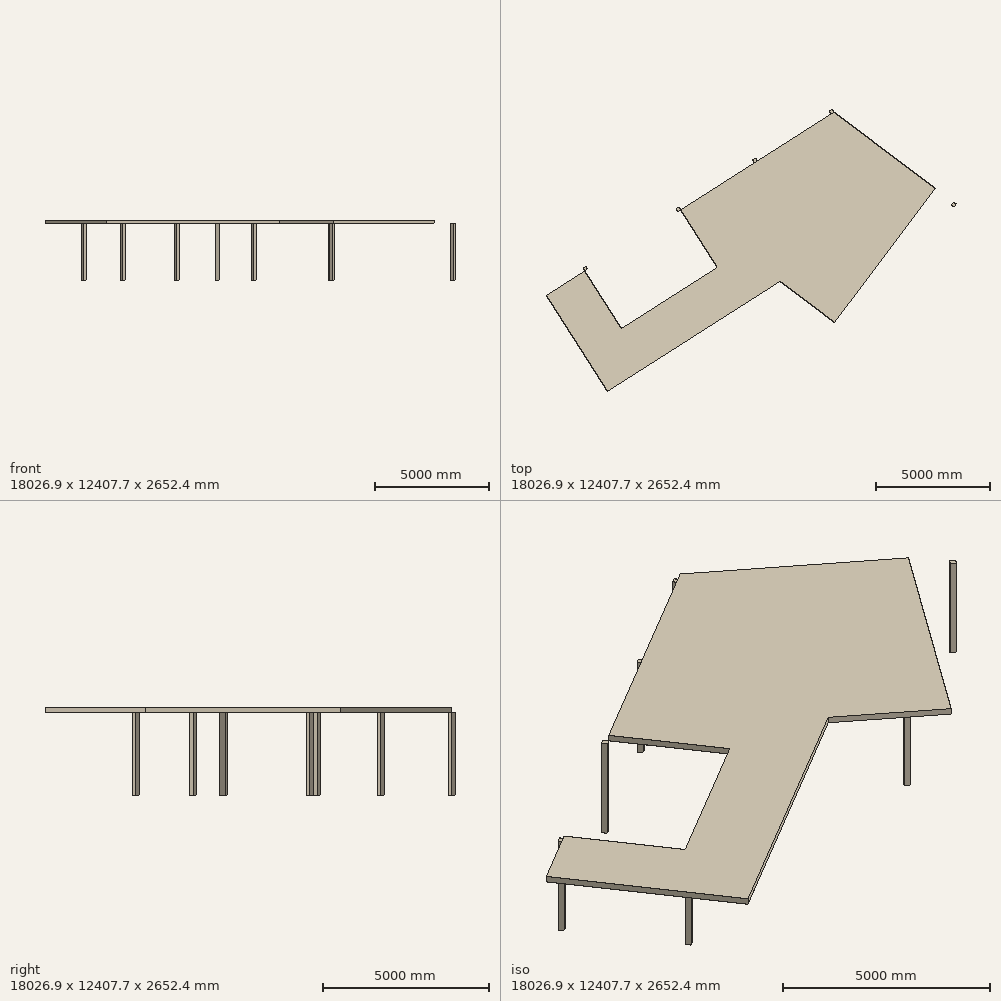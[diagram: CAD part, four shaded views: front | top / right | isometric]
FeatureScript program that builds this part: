
annotation { "Feature Type Name" : "Feature", "Feature Type Description" : "" }
export const myFeature = defineFeature(function(context is Context, id is Id, definition is map)
    precondition{}
    {
        {
            var Q0;
            Q0=qCreatedBy(makeId("Top.planeOp"),FACE);
            var sketch = newSketch(context, id + "F0", { "sketchPlane" : qUnion([Q0])});
            skLineSegment(sketch, "E0", {"start": v(-11635.93, 4721.16) * mm, "end": v(-8948.27, 504.95) * mm});
            skLineSegment(sketch, "E1", {"start": v(-8948.27, 504.95) * mm, "end": v(-1359.08, 5342.74) * mm});
            skLineSegment(sketch, "E2", {"start": v(-1359.08, 5342.74) * mm, "end": v(-4046.74, 9558.96) * mm});
            skLineSegment(sketch, "E3", {"start": v(-4046.74, 9558.96) * mm, "end": v(-5733.23, 8483.9) * mm});
            skLineSegment(sketch, "E4", {"start": v(-1359.08, 5342.74) * mm, "end": v(1038.57, 3539.62) * mm});
            skLineSegment(sketch, "E5", {"start": v(1038.57, 3539.62) * mm, "end": v(5469.96, 9432.14) * mm});
            skLineSegment(sketch, "E6", {"start": v(5469.96, 9432.14) * mm, "end": v(3072.3, 11235.27) * mm});
            skLineSegment(sketch, "E7", {"start": v(-4046.74, 9558.96) * mm, "end": v(1012.71, 12784.15) * mm});
            skLineSegment(sketch, "E8", {"start": v(1012.71, 12784.15) * mm, "end": v(3072.3, 11235.27) * mm});
            skLineSegment(sketch, "E9", {"start": v(-11098.4, 3877.92) * mm, "end": v(-9411.91, 4952.99) * mm});
            skLineSegment(sketch, "E10", {"start": v(-10560.87, 3034.68) * mm, "end": v(-8874.38, 4109.74) * mm});
            skLineSegment(sketch, "E11", {"start": v(-10023.33, 2191.43) * mm, "end": v(-8336.85, 3266.5) * mm});
            skLineSegment(sketch, "E12", {"start": v(-9485.8, 1348.2) * mm, "end": v(-1222.02, 6616) * mm});
            skLineSegment(sketch, "E13", {"start": v(239.36, 4140.66) * mm, "end": v(4670.74, 10033.19) * mm});
            skLineSegment(sketch, "E14", {"start": v(-559.86, 4741.7) * mm, "end": v(3871.52, 10634.23) * mm});
            skLineSegment(sketch, "E15", {"start": v(-10792.69, 5258.7) * mm, "end": v(-8105.03, 1042.48) * mm});
            skLineSegment(sketch, "E16", {"start": v(-9949.45, 5796.23) * mm, "end": v(-7261.78, 1580.01) * mm});
            skLineSegment(sketch, "E17", {"start": v(-7493.6, 3804.03) * mm, "end": v(-6418.54, 2117.55) * mm});
            skLineSegment(sketch, "E18", {"start": v(-6650.36, 4341.56) * mm, "end": v(-5575.3, 2655.08) * mm});
            skLineSegment(sketch, "E19", {"start": v(-5807.12, 4879.1) * mm, "end": v(-4732.05, 3192.61) * mm});
            skLineSegment(sketch, "E20", {"start": v(-4963.88, 5416.63) * mm, "end": v(-3888.81, 3730.14) * mm});
            skLineSegment(sketch, "E21", {"start": v(-5733.23, 8483.9) * mm, "end": v(-3045.57, 4267.68) * mm});
            skLineSegment(sketch, "E22", {"start": v(-4889.99, 9021.42) * mm, "end": v(-2202.32, 4805.2) * mm});
            skLineSegment(sketch, "E23.trimOffspring", {"start": v(-7493.6, 3804.03) * mm, "end": v(-1084.96, 7889.28) * mm});
            skLineSegment(sketch, "E24.trimOffspring", {"start": v(-9949.45, 5796.23) * mm, "end": v(-11635.93, 4721.16) * mm});
            skLineSegment(sketch, "E25.trimOffspring", {"start": v(-5195.7, 7640.65) * mm, "end": v(-810.83, 10435.82) * mm});
            skLineSegment(sketch, "E26.trimOffspring", {"start": v(-4658.16, 6797.4) * mm, "end": v(-947.9, 9162.55) * mm});
            skLineSegment(sketch, "E27", {"start": v(-8336.85, 3266.5) * mm, "end": v(-7493.6, 3804.03) * mm});
            skLineSegment(sketch, "E28", {"start": v(-1359.08, 5342.74) * mm, "end": v(3072.3, 11235.27) * mm});
            skPoint(sketch, "E29.orphan", {"position": v(0, 12138.59) * mm});
            skLineSegment(sketch, "E30", {"start": v(-1222.02, 6616) * mm, "end": v(1699.72, 4418.76) * mm});
            skLineSegment(sketch, "E31", {"start": v(-1084.96, 7889.28) * mm, "end": v(2360.86, 5297.9) * mm});
            skLineSegment(sketch, "E32", {"start": v(-947.9, 9162.55) * mm, "end": v(3022, 6177.04) * mm});
            skLineSegment(sketch, "E33", {"start": v(-810.83, 10435.82) * mm, "end": v(3683.15, 7056.18) * mm});
            skLineSegment(sketch, "E34", {"start": v(-673.77, 11709.09) * mm, "end": v(4344.3, 7935.32) * mm});
            skLineSegment(sketch, "E35", {"start": v(4945.34, 8734.54) * mm, "end": v(226.72, 12283.1) * mm});
            skLineSegment(sketch, "E36", {"start": v(-1359.08, 5342.74) * mm, "end": v(-673.77, 11709.09) * mm});
            skLineSegment(sketch, "E37", {"start": v(1012.71, 12784.15) * mm, "end": v(-1359.08, 5342.74) * mm});
            skLineSegment(sketch, "E38", {"start": v(-1359.08, 5342.74) * mm, "end": v(-2606, 10477.36) * mm});
            skLineSegment(sketch, "E39", {"start": v(2042.5, 12009.7) * mm, "end": v(-1359.08, 5342.74) * mm});
            skSolve(sketch);
        }
        {
            var Q0;
            {var subQ0=sQuery(id+"F0.wireOp",EDGE,"E24.trimOffspring");var subQ1=sQuery(id+"F0.wireOp",EDGE,"E0");var subQ2=makeQuery(id+"F0.imprint","INTERSECT",VERTEX,{"derivedFrom":[subQ1,subQ0]});Q0=makeQuery(id+"F0.imprint","IMPRINT",FACE,{"disambiguationData":[TD([[makeQuery(id+"F0.imprint","IMPRINT",EDGE,{"disambiguationData":[TD([[subQ2,-1.0]])],"derivedFrom":subQ1}),1.0]])]});}
            var Q1;
            {var subQ0=sQuery(id+"F0.wireOp",EDGE,"E16");var subQ1=sQuery(id+"F0.wireOp",EDGE,"E9");var subQ2=makeQuery(id+"F0.imprint","INTERSECT",VERTEX,{"derivedFrom":[subQ1,subQ0]});Q1=makeQuery(id+"F0.imprint","IMPRINT",FACE,{"disambiguationData":[TD([[makeQuery(id+"F0.imprint","IMPRINT",EDGE,{"disambiguationData":[TD([[subQ2,1.0]])],"derivedFrom":subQ1}),1.0]])]});}
            var Q2;
            {var subQ0=sQuery(id+"F0.wireOp",EDGE,"E16");var subQ1=sQuery(id+"F0.wireOp",EDGE,"E9");var subQ2=makeQuery(id+"F0.imprint","INTERSECT",VERTEX,{"derivedFrom":[subQ1,subQ0]});Q2=makeQuery(id+"F0.imprint","IMPRINT",FACE,{"disambiguationData":[TD([[makeQuery(id+"F0.imprint","IMPRINT",EDGE,{"disambiguationData":[TD([[subQ2,1.0]])],"derivedFrom":subQ1}),-1.0]])]});}
            var Q3;
            {var subQ0=sQuery(id+"F0.wireOp",EDGE,"E9");var subQ1=sQuery(id+"F0.wireOp",EDGE,"E0");var subQ2=makeQuery(id+"F0.imprint","INTERSECT",VERTEX,{"derivedFrom":[subQ1,subQ0]});Q3=makeQuery(id+"F0.imprint","IMPRINT",FACE,{"disambiguationData":[TD([[makeQuery(id+"F0.imprint","IMPRINT",EDGE,{"disambiguationData":[TD([[subQ2,-1.0]])],"derivedFrom":subQ1}),1.0]])]});}
            var Q4;
            {var subQ0=sQuery(id+"F0.wireOp",EDGE,"E10");var subQ1=sQuery(id+"F0.wireOp",EDGE,"E0");var subQ2=makeQuery(id+"F0.imprint","INTERSECT",VERTEX,{"derivedFrom":[subQ1,subQ0]});Q4=makeQuery(id+"F0.imprint","IMPRINT",FACE,{"disambiguationData":[TD([[makeQuery(id+"F0.imprint","IMPRINT",EDGE,{"disambiguationData":[TD([[subQ2,-1.0]])],"derivedFrom":subQ1}),1.0]])]});}
            var Q5;
            {var subQ0=sQuery(id+"F0.wireOp",EDGE,"E16");var subQ1=sQuery(id+"F0.wireOp",EDGE,"E10");var subQ2=makeQuery(id+"F0.imprint","INTERSECT",VERTEX,{"derivedFrom":[subQ1,subQ0]});Q5=makeQuery(id+"F0.imprint","IMPRINT",FACE,{"disambiguationData":[TD([[makeQuery(id+"F0.imprint","IMPRINT",EDGE,{"disambiguationData":[TD([[subQ2,1.0]])],"derivedFrom":subQ1}),-1.0]])]});}
            var Q6;
            {var subQ3=sQuery(id+"F0.wireOp",EDGE,"E15");var subQ5=sQuery(id+"F0.wireOp",EDGE,"E12");var subQ6=makeQuery(id+"F0.imprint","INTERSECT",VERTEX,{"derivedFrom":[subQ5,subQ3]});Q6=makeQuery(id+"F0.imprint","IMPRINT",FACE,{"disambiguationData":[TD([[makeQuery(id+"F0.imprint","IMPRINT",EDGE,{"disambiguationData":[TD([[subQ6,-1.0]])],"derivedFrom":subQ5}),1.0]])]});}
            var Q7;
            {var subQ0=sQuery(id+"F0.wireOp",EDGE,"E11");var subQ1=sQuery(id+"F0.wireOp",EDGE,"E0");var subQ2=makeQuery(id+"F0.imprint","INTERSECT",VERTEX,{"derivedFrom":[subQ1,subQ0]});Q7=makeQuery(id+"F0.imprint","IMPRINT",FACE,{"disambiguationData":[TD([[makeQuery(id+"F0.imprint","IMPRINT",EDGE,{"disambiguationData":[TD([[subQ2,-1.0]])],"derivedFrom":subQ1}),1.0]])]});}
            var Q8;
            {var subQ0=sQuery(id+"F0.wireOp",EDGE,"E1");var subQ1=sQuery(id+"F0.wireOp",EDGE,"E0");var subQ2=makeQuery(id+"F0.imprint","INTERSECT",VERTEX,{"derivedFrom":[subQ1,subQ0]});Q8=makeQuery(id+"F0.imprint","IMPRINT",FACE,{"disambiguationData":[TD([[makeQuery(id+"F0.imprint","IMPRINT",EDGE,{"disambiguationData":[TD([[subQ2,1.0]])],"derivedFrom":subQ1}),1.0]])]});}
            var Q9;
            {var subQ5=sQuery(id+"F0.wireOp",EDGE,"E27");Q9=makeQuery(id+"F0.imprint","IMPRINT",FACE,{"disambiguationData":[TD([[makeQuery(id+"F0.imprint","IMPRINT",EDGE,{"derivedFrom":subQ5}),-1.0]])]});}
            var Q10;
            {var subQ0=sQuery(id+"F0.wireOp",EDGE,"E17");var subQ1=sQuery(id+"F0.wireOp",EDGE,"E12");var subQ2=makeQuery(id+"F0.imprint","INTERSECT",VERTEX,{"derivedFrom":[subQ1,subQ0]});Q10=makeQuery(id+"F0.imprint","IMPRINT",FACE,{"disambiguationData":[TD([[makeQuery(id+"F0.imprint","IMPRINT",EDGE,{"disambiguationData":[TD([[subQ2,-1.0]])],"derivedFrom":subQ1}),1.0]])]});}
            var Q11;
            {var subQ0=sQuery(id+"F0.wireOp",EDGE,"E18");var subQ1=sQuery(id+"F0.wireOp",EDGE,"E12");var subQ2=makeQuery(id+"F0.imprint","INTERSECT",VERTEX,{"derivedFrom":[subQ1,subQ0]});Q11=makeQuery(id+"F0.imprint","IMPRINT",FACE,{"disambiguationData":[TD([[makeQuery(id+"F0.imprint","IMPRINT",EDGE,{"disambiguationData":[TD([[subQ2,-1.0]])],"derivedFrom":subQ1}),1.0]])]});}
            var Q12;
            {var subQ0=sQuery(id+"F0.wireOp",EDGE,"E19");var subQ1=sQuery(id+"F0.wireOp",EDGE,"E12");var subQ2=makeQuery(id+"F0.imprint","INTERSECT",VERTEX,{"derivedFrom":[subQ1,subQ0]});Q12=makeQuery(id+"F0.imprint","IMPRINT",FACE,{"disambiguationData":[TD([[makeQuery(id+"F0.imprint","IMPRINT",EDGE,{"disambiguationData":[TD([[subQ2,-1.0]])],"derivedFrom":subQ1}),1.0]])]});}
            var Q13;
            {var subQ0=sQuery(id+"F0.wireOp",EDGE,"E20");var subQ1=sQuery(id+"F0.wireOp",EDGE,"E12");var subQ2=makeQuery(id+"F0.imprint","INTERSECT",VERTEX,{"derivedFrom":[subQ1,subQ0]});Q13=makeQuery(id+"F0.imprint","IMPRINT",FACE,{"disambiguationData":[TD([[makeQuery(id+"F0.imprint","IMPRINT",EDGE,{"disambiguationData":[TD([[subQ2,-1.0]])],"derivedFrom":subQ1}),1.0]])]});}
            var Q14;
            {var subQ0=sQuery(id+"F0.wireOp",EDGE,"E21");var subQ1=sQuery(id+"F0.wireOp",EDGE,"E12");var subQ2=makeQuery(id+"F0.imprint","INTERSECT",VERTEX,{"derivedFrom":[subQ1,subQ0]});Q14=makeQuery(id+"F0.imprint","IMPRINT",FACE,{"disambiguationData":[TD([[makeQuery(id+"F0.imprint","IMPRINT",EDGE,{"disambiguationData":[TD([[subQ2,-1.0]])],"derivedFrom":subQ1}),1.0]])]});}
            var Q15;
            {var subQ0=sQuery(id+"F0.wireOp",EDGE,"E26.trimOffspring");var subQ1=sQuery(id+"F0.wireOp",EDGE,"E21");var subQ2=makeQuery(id+"F0.imprint","INTERSECT",VERTEX,{"derivedFrom":[subQ1,subQ0]});Q15=makeQuery(id+"F0.imprint","IMPRINT",FACE,{"disambiguationData":[TD([[makeQuery(id+"F0.imprint","IMPRINT",EDGE,{"disambiguationData":[TD([[subQ2,-1.0]])],"derivedFrom":subQ1}),1.0]])]});}
            var Q16;
            {var subQ0=sQuery(id+"F0.wireOp",EDGE,"E25.trimOffspring");var subQ1=sQuery(id+"F0.wireOp",EDGE,"E21");var subQ2=makeQuery(id+"F0.imprint","INTERSECT",VERTEX,{"derivedFrom":[subQ1,subQ0]});Q16=makeQuery(id+"F0.imprint","IMPRINT",FACE,{"disambiguationData":[TD([[makeQuery(id+"F0.imprint","IMPRINT",EDGE,{"disambiguationData":[TD([[subQ2,-1.0]])],"derivedFrom":subQ1}),1.0]])]});}
            var Q17;
            {var subQ0=sQuery(id+"F0.wireOp",EDGE,"E21");var subQ1=sQuery(id+"F0.wireOp",EDGE,"E3");var subQ2=makeQuery(id+"F0.imprint","INTERSECT",VERTEX,{"derivedFrom":[subQ1,subQ0]});Q17=makeQuery(id+"F0.imprint","IMPRINT",FACE,{"disambiguationData":[TD([[makeQuery(id+"F0.imprint","IMPRINT",EDGE,{"disambiguationData":[TD([[subQ2,1.0]])],"derivedFrom":subQ1}),1.0]])]});}
            var Q18;
            {var subQ0=sQuery(id+"F0.wireOp",EDGE,"E3");var subQ5=sQuery(id+"F0.wireOp",EDGE,"E22");var subQ6=makeQuery(id+"F0.imprint","INTERSECT",VERTEX,{"derivedFrom":[subQ0,subQ5]});Q18=makeQuery(id+"F0.imprint","IMPRINT",FACE,{"disambiguationData":[TD([[makeQuery(id+"F0.imprint","IMPRINT",EDGE,{"disambiguationData":[TD([[subQ6,-1.0]])],"derivedFrom":subQ5}),1.0]])]});}
            var Q19;
            {var subQ1=sQuery(id+"F0.wireOp",EDGE,"E2");var subQ3=sQuery(id+"F0.wireOp",EDGE,"E25.trimOffspring");var subQ4=makeQuery(id+"F0.imprint","INTERSECT",VERTEX,{"derivedFrom":[subQ1,subQ3]});Q19=makeQuery(id+"F0.imprint","IMPRINT",FACE,{"disambiguationData":[TD([[makeQuery(id+"F0.imprint","IMPRINT",EDGE,{"disambiguationData":[TD([[subQ4,-1.0]])],"derivedFrom":subQ3}),1.0]])]});}
            var Q20;
            {var subQ0=sQuery(id+"F0.wireOp",EDGE,"ySlomsGb-js9K-Jc3M-ecpa-KJbRU4JIcBsO");var subQ1=sQuery(id+"F0.wireOp",EDGE,"E7");var subQ2=makeQuery(id+"F0.imprint","INTERSECT",VERTEX,{"derivedFrom":[subQ1,subQ0]});Q20=makeQuery(id+"F0.imprint","IMPRINT",FACE,{"disambiguationData":[TD([[makeQuery(id+"F0.imprint","IMPRINT",EDGE,{"disambiguationData":[TD([[subQ2,1.0]])],"derivedFrom":subQ0}),-1.0]])]});}
            var Q21;
            {var subQ0=sQuery(id+"F0.wireOp",EDGE,"E34");var subQ3=sQuery(id+"F0.wireOp",EDGE,"ZUNuRMhS-ujy8-TC27-MlvK-OisAggV88Hkc");var subQ5=makeQuery(id+"F0.imprint","INTERSECT",VERTEX,{"derivedFrom":[subQ0,subQ3]});Q21=makeQuery(id+"F0.imprint","IMPRINT",FACE,{"disambiguationData":[TD([[makeQuery(id+"F0.imprint","IMPRINT",EDGE,{"disambiguationData":[TD([[subQ5,1.0]])],"derivedFrom":subQ0}),1.0]])]});}
            var Q22;
            {var subQ0=sQuery(id+"F0.wireOp",EDGE,"lfVSc5wO-GHd6-1YIc-mb3Z-fNhNrwEVWLqH");var subQ3=sQuery(id+"F0.wireOp",EDGE,"E35");var subQ5=makeQuery(id+"F0.imprint","INTERSECT",VERTEX,{"derivedFrom":[subQ0,subQ3]});Q22=makeQuery(id+"F0.imprint","IMPRINT",FACE,{"disambiguationData":[TD([[makeQuery(id+"F0.imprint","IMPRINT",EDGE,{"disambiguationData":[TD([[subQ5,-1.0]])],"derivedFrom":subQ0}),1.0]])]});}
            var Q23;
            {var subQ0=sQuery(id+"F0.wireOp",EDGE,"E8");var subQ5=sQuery(id+"F0.wireOp",EDGE,"k5RD2hiX-lBWQ-B76e-Ko6Y-DRXfyth6Ei6H");var subQ6=makeQuery(id+"F0.imprint","INTERSECT",VERTEX,{"derivedFrom":[subQ0,subQ5]});Q23=makeQuery(id+"F0.imprint","IMPRINT",FACE,{"disambiguationData":[TD([[makeQuery(id+"F0.imprint","IMPRINT",EDGE,{"disambiguationData":[TD([[subQ6,1.0]])],"derivedFrom":subQ5}),1.0]])]});}
            var Q24;
            {var subQ1=sQuery(id+"F0.wireOp",EDGE,"E8");var subQ3=sQuery(id+"F0.wireOp",EDGE,"k5RD2hiX-lBWQ-B76e-Ko6Y-DRXfyth6Ei6H");var subQ4=makeQuery(id+"F0.imprint","INTERSECT",VERTEX,{"derivedFrom":[subQ1,subQ3]});Q24=makeQuery(id+"F0.imprint","IMPRINT",FACE,{"disambiguationData":[TD([[makeQuery(id+"F0.imprint","IMPRINT",EDGE,{"disambiguationData":[TD([[subQ4,1.0]])],"derivedFrom":subQ3}),-1.0]])]});}
            var Q25;
            {var subQ1=sQuery(id+"F0.wireOp",EDGE,"E6");var subQ3=sQuery(id+"F0.wireOp",EDGE,"E14");var subQ4=makeQuery(id+"F0.imprint","INTERSECT",VERTEX,{"derivedFrom":[subQ1,subQ3]});Q25=makeQuery(id+"F0.imprint","IMPRINT",FACE,{"disambiguationData":[TD([[makeQuery(id+"F0.imprint","IMPRINT",EDGE,{"disambiguationData":[TD([[subQ4,1.0]])],"derivedFrom":subQ3}),1.0]])]});}
            var Q26;
            {var subQ0=sQuery(id+"F0.wireOp",EDGE,"E13");var subQ1=sQuery(id+"F0.wireOp",EDGE,"E6");var subQ2=makeQuery(id+"F0.imprint","INTERSECT",VERTEX,{"derivedFrom":[subQ1,subQ0]});Q26=makeQuery(id+"F0.imprint","IMPRINT",FACE,{"disambiguationData":[TD([[makeQuery(id+"F0.imprint","IMPRINT",EDGE,{"disambiguationData":[TD([[subQ2,-1.0]])],"derivedFrom":subQ1}),1.0]])]});}
            var Q27;
            {var subQ0=sQuery(id+"F0.wireOp",EDGE,"E6");var subQ1=sQuery(id+"F0.wireOp",EDGE,"E5");var subQ2=makeQuery(id+"F0.imprint","INTERSECT",VERTEX,{"derivedFrom":[subQ1,subQ0]});Q27=makeQuery(id+"F0.imprint","IMPRINT",FACE,{"disambiguationData":[TD([[makeQuery(id+"F0.imprint","IMPRINT",EDGE,{"disambiguationData":[TD([[subQ2,1.0]])],"derivedFrom":subQ1}),1.0]])]});}
            var Q28;
            {var subQ0=sQuery(id+"F0.wireOp",EDGE,"E33");var subQ5=sQuery(id+"F0.wireOp",EDGE,"ZUNuRMhS-ujy8-TC27-MlvK-OisAggV88Hkc");var subQ6=makeQuery(id+"F0.imprint","INTERSECT",VERTEX,{"derivedFrom":[subQ0,subQ5]});Q28=makeQuery(id+"F0.imprint","IMPRINT",FACE,{"disambiguationData":[TD([[makeQuery(id+"F0.imprint","IMPRINT",EDGE,{"disambiguationData":[TD([[subQ6,1.0]])],"derivedFrom":subQ5}),-1.0]])]});}
            var Q29;
            {var subQ0=sQuery(id+"F0.wireOp",EDGE,"E34");var subQ1=sQuery(id+"F0.wireOp",EDGE,"lfVSc5wO-GHd6-1YIc-mb3Z-fNhNrwEVWLqH");var subQ2=makeQuery(id+"F0.imprint","INTERSECT",VERTEX,{"derivedFrom":[subQ1,subQ0]});Q29=makeQuery(id+"F0.imprint","IMPRINT",FACE,{"disambiguationData":[TD([[makeQuery(id+"F0.imprint","IMPRINT",EDGE,{"disambiguationData":[TD([[subQ2,-1.0]])],"derivedFrom":subQ1}),1.0]])]});}
            var Q30;
            {var subQ0=sQuery(id+"F0.wireOp",EDGE,"E34");var subQ1=sQuery(id+"F0.wireOp",EDGE,"lfVSc5wO-GHd6-1YIc-mb3Z-fNhNrwEVWLqH");var subQ2=makeQuery(id+"F0.imprint","INTERSECT",VERTEX,{"derivedFrom":[subQ1,subQ0]});Q30=makeQuery(id+"F0.imprint","IMPRINT",FACE,{"disambiguationData":[TD([[makeQuery(id+"F0.imprint","IMPRINT",EDGE,{"disambiguationData":[TD([[subQ2,-1.0]])],"derivedFrom":subQ1}),-1.0]])]});}
            var Q31;
            {var subQ0=sQuery(id+"F0.wireOp",EDGE,"E5");var subQ1=sQuery(id+"F0.wireOp",EDGE,"E4");var subQ2=makeQuery(id+"F0.imprint","INTERSECT",VERTEX,{"derivedFrom":[subQ1,subQ0]});Q31=makeQuery(id+"F0.imprint","IMPRINT",FACE,{"disambiguationData":[TD([[makeQuery(id+"F0.imprint","IMPRINT",EDGE,{"disambiguationData":[TD([[subQ2,1.0]])],"derivedFrom":subQ1}),1.0]])]});}
            var Q32;
            {var subQ0=sQuery(id+"F0.wireOp",EDGE,"E13");var subQ1=sQuery(id+"F0.wireOp",EDGE,"E4");var subQ2=makeQuery(id+"F0.imprint","INTERSECT",VERTEX,{"derivedFrom":[subQ1,subQ0]});Q32=makeQuery(id+"F0.imprint","IMPRINT",FACE,{"disambiguationData":[TD([[makeQuery(id+"F0.imprint","IMPRINT",EDGE,{"disambiguationData":[TD([[subQ2,1.0]])],"derivedFrom":subQ1}),1.0]])]});}
            var Q33;
            {var subQ0=sQuery(id+"F0.wireOp",EDGE,"E15");var subQ1=sQuery(id+"F0.wireOp",EDGE,"E1");var subQ2=makeQuery(id+"F0.imprint","INTERSECT",VERTEX,{"derivedFrom":[subQ1,subQ0]});Q33=makeQuery(id+"F0.imprint","IMPRINT",FACE,{"disambiguationData":[TD([[makeQuery(id+"F0.imprint","IMPRINT",EDGE,{"disambiguationData":[TD([[subQ2,-1.0]])],"derivedFrom":subQ1}),1.0]])]});}
            var Q34;
            {var subQ0=sQuery(id+"F0.wireOp",EDGE,"E16");var subQ1=sQuery(id+"F0.wireOp",EDGE,"E1");var subQ2=makeQuery(id+"F0.imprint","INTERSECT",VERTEX,{"derivedFrom":[subQ1,subQ0]});Q34=makeQuery(id+"F0.imprint","IMPRINT",FACE,{"disambiguationData":[TD([[makeQuery(id+"F0.imprint","IMPRINT",EDGE,{"disambiguationData":[TD([[subQ2,-1.0]])],"derivedFrom":subQ1}),1.0]])]});}
            var Q35;
            {var subQ0=sQuery(id+"F0.wireOp",EDGE,"E17");var subQ1=sQuery(id+"F0.wireOp",EDGE,"E1");var subQ2=makeQuery(id+"F0.imprint","INTERSECT",VERTEX,{"derivedFrom":[subQ1,subQ0]});Q35=makeQuery(id+"F0.imprint","IMPRINT",FACE,{"disambiguationData":[TD([[makeQuery(id+"F0.imprint","IMPRINT",EDGE,{"disambiguationData":[TD([[subQ2,-1.0]])],"derivedFrom":subQ1}),1.0]])]});}
            var Q36;
            {var subQ0=sQuery(id+"F0.wireOp",EDGE,"E18");var subQ1=sQuery(id+"F0.wireOp",EDGE,"E1");var subQ2=makeQuery(id+"F0.imprint","INTERSECT",VERTEX,{"derivedFrom":[subQ1,subQ0]});Q36=makeQuery(id+"F0.imprint","IMPRINT",FACE,{"disambiguationData":[TD([[makeQuery(id+"F0.imprint","IMPRINT",EDGE,{"disambiguationData":[TD([[subQ2,-1.0]])],"derivedFrom":subQ1}),1.0]])]});}
            var Q37;
            {var subQ0=sQuery(id+"F0.wireOp",EDGE,"E19");var subQ1=sQuery(id+"F0.wireOp",EDGE,"E1");var subQ2=makeQuery(id+"F0.imprint","INTERSECT",VERTEX,{"derivedFrom":[subQ1,subQ0]});Q37=makeQuery(id+"F0.imprint","IMPRINT",FACE,{"disambiguationData":[TD([[makeQuery(id+"F0.imprint","IMPRINT",EDGE,{"disambiguationData":[TD([[subQ2,-1.0]])],"derivedFrom":subQ1}),1.0]])]});}
            var Q38;
            {var subQ0=sQuery(id+"F0.wireOp",EDGE,"E20");var subQ1=sQuery(id+"F0.wireOp",EDGE,"E1");var subQ2=makeQuery(id+"F0.imprint","INTERSECT",VERTEX,{"derivedFrom":[subQ1,subQ0]});Q38=makeQuery(id+"F0.imprint","IMPRINT",FACE,{"disambiguationData":[TD([[makeQuery(id+"F0.imprint","IMPRINT",EDGE,{"disambiguationData":[TD([[subQ2,-1.0]])],"derivedFrom":subQ1}),1.0]])]});}
            var Q39;
            {var subQ0=sQuery(id+"F0.wireOp",EDGE,"E21");var subQ1=sQuery(id+"F0.wireOp",EDGE,"E1");var subQ2=makeQuery(id+"F0.imprint","INTERSECT",VERTEX,{"derivedFrom":[subQ1,subQ0]});Q39=makeQuery(id+"F0.imprint","IMPRINT",FACE,{"disambiguationData":[TD([[makeQuery(id+"F0.imprint","IMPRINT",EDGE,{"disambiguationData":[TD([[subQ2,-1.0]])],"derivedFrom":subQ1}),1.0]])]});}
            var Q40;
            {var subQ0=sQuery(id+"F0.wireOp",EDGE,"E26.trimOffspring");var subQ1=sQuery(id+"F0.wireOp",EDGE,"E2");var subQ2=makeQuery(id+"F0.imprint","INTERSECT",VERTEX,{"derivedFrom":[subQ1,subQ0]});Q40=makeQuery(id+"F0.imprint","IMPRINT",FACE,{"disambiguationData":[TD([[makeQuery(id+"F0.imprint","IMPRINT",EDGE,{"disambiguationData":[TD([[subQ2,-1.0]])],"derivedFrom":subQ1}),1.0]])]});}
            var Q41;
            {var subQ0=sQuery(id+"F0.wireOp",EDGE,"E23.trimOffspring");var subQ1=sQuery(id+"F0.wireOp",EDGE,"E2");var subQ2=makeQuery(id+"F0.imprint","INTERSECT",VERTEX,{"derivedFrom":[subQ1,subQ0]});Q41=makeQuery(id+"F0.imprint","IMPRINT",FACE,{"disambiguationData":[TD([[makeQuery(id+"F0.imprint","IMPRINT",EDGE,{"disambiguationData":[TD([[subQ2,-1.0]])],"derivedFrom":subQ1}),1.0]])]});}
            var Q42;
            {var subQ0=sQuery(id+"F0.wireOp",EDGE,"E12");var subQ1=sQuery(id+"F0.wireOp",EDGE,"E2");var subQ2=makeQuery(id+"F0.imprint","INTERSECT",VERTEX,{"derivedFrom":[subQ1,subQ0]});Q42=makeQuery(id+"F0.imprint","IMPRINT",FACE,{"disambiguationData":[TD([[makeQuery(id+"F0.imprint","IMPRINT",EDGE,{"disambiguationData":[TD([[subQ2,-1.0]])],"derivedFrom":subQ1}),1.0]])]});}
            var Q43;
            {var subQ0=sQuery(id+"F0.wireOp",EDGE,"E2");var subQ5=sQuery(id+"F0.wireOp",EDGE,"E12");var subQ6=makeQuery(id+"F0.imprint","INTERSECT",VERTEX,{"derivedFrom":[subQ0,subQ5]});Q43=makeQuery(id+"F0.imprint","IMPRINT",FACE,{"disambiguationData":[TD([[makeQuery(id+"F0.imprint","IMPRINT",EDGE,{"disambiguationData":[TD([[subQ6,1.0]])],"derivedFrom":subQ5}),-1.0]])]});}
            var Q44;
            {var subQ0=sQuery(id+"F0.wireOp",EDGE,"E26.trimOffspring");var subQ1=sQuery(id+"F0.wireOp",EDGE,"E2");var subQ2=makeQuery(id+"F0.imprint","INTERSECT",VERTEX,{"derivedFrom":[subQ1,subQ0]});Q44=makeQuery(id+"F0.imprint","IMPRINT",FACE,{"disambiguationData":[TD([[makeQuery(id+"F0.imprint","IMPRINT",EDGE,{"disambiguationData":[TD([[subQ2,-1.0]])],"derivedFrom":subQ1}),-1.0]])]});}
            var Q45;
            {var subQ1=sQuery(id+"F0.wireOp",EDGE,"E25.trimOffspring");var subQ3=sQuery(id+"F0.wireOp",EDGE,"ySlomsGb-js9K-Jc3M-ecpa-KJbRU4JIcBsO");var subQ4=makeQuery(id+"F0.imprint","INTERSECT",VERTEX,{"derivedFrom":[subQ1,subQ3]});Q45=makeQuery(id+"F0.imprint","IMPRINT",FACE,{"disambiguationData":[TD([[makeQuery(id+"F0.imprint","IMPRINT",EDGE,{"disambiguationData":[TD([[subQ4,1.0]])],"derivedFrom":subQ3}),-1.0]])]});}
            var Q46;
            {var subQ3=sQuery(id+"F0.wireOp",EDGE,"E32");var subQ5=sQuery(id+"F0.wireOp",EDGE,"ZUNuRMhS-ujy8-TC27-MlvK-OisAggV88Hkc");var subQ6=makeQuery(id+"F0.imprint","INTERSECT",VERTEX,{"derivedFrom":[subQ3,subQ5]});Q46=makeQuery(id+"F0.imprint","IMPRINT",FACE,{"disambiguationData":[TD([[makeQuery(id+"F0.imprint","IMPRINT",EDGE,{"disambiguationData":[TD([[subQ6,1.0]])],"derivedFrom":subQ5}),-1.0]])]});}
            var Q47;
            {var subQ0=sQuery(id+"F0.wireOp",EDGE,"E33");var subQ1=sQuery(id+"F0.wireOp",EDGE,"lfVSc5wO-GHd6-1YIc-mb3Z-fNhNrwEVWLqH");var subQ2=makeQuery(id+"F0.imprint","INTERSECT",VERTEX,{"derivedFrom":[subQ1,subQ0]});Q47=makeQuery(id+"F0.imprint","IMPRINT",FACE,{"disambiguationData":[TD([[makeQuery(id+"F0.imprint","IMPRINT",EDGE,{"disambiguationData":[TD([[subQ2,-1.0]])],"derivedFrom":subQ1}),1.0]])]});}
            var Q48;
            {var subQ0=sQuery(id+"F0.wireOp",EDGE,"E33");var subQ1=sQuery(id+"F0.wireOp",EDGE,"lfVSc5wO-GHd6-1YIc-mb3Z-fNhNrwEVWLqH");var subQ2=makeQuery(id+"F0.imprint","INTERSECT",VERTEX,{"derivedFrom":[subQ1,subQ0]});Q48=makeQuery(id+"F0.imprint","IMPRINT",FACE,{"disambiguationData":[TD([[makeQuery(id+"F0.imprint","IMPRINT",EDGE,{"disambiguationData":[TD([[subQ2,-1.0]])],"derivedFrom":subQ1}),-1.0]])]});}
            var Q49;
            {var subQ0=sQuery(id+"F0.wireOp",EDGE,"E34");var subQ1=sQuery(id+"F0.wireOp",EDGE,"E28");var subQ2=makeQuery(id+"F0.imprint","INTERSECT",VERTEX,{"derivedFrom":[subQ1,subQ0]});Q49=makeQuery(id+"F0.imprint","IMPRINT",FACE,{"disambiguationData":[TD([[makeQuery(id+"F0.imprint","IMPRINT",EDGE,{"disambiguationData":[TD([[subQ2,-1.0]])],"derivedFrom":subQ1}),1.0]])]});}
            var Q50;
            {var subQ0=sQuery(id+"F0.wireOp",EDGE,"E34");var subQ1=sQuery(id+"F0.wireOp",EDGE,"E14");var subQ2=makeQuery(id+"F0.imprint","INTERSECT",VERTEX,{"derivedFrom":[subQ1,subQ0]});Q50=makeQuery(id+"F0.imprint","IMPRINT",FACE,{"disambiguationData":[TD([[makeQuery(id+"F0.imprint","IMPRINT",EDGE,{"disambiguationData":[TD([[subQ2,-1.0]])],"derivedFrom":subQ1}),1.0]])]});}
            var Q51;
            {var subQ0=sQuery(id+"F0.wireOp",EDGE,"E34");var subQ1=sQuery(id+"F0.wireOp",EDGE,"E13");var subQ2=makeQuery(id+"F0.imprint","INTERSECT",VERTEX,{"derivedFrom":[subQ1,subQ0]});Q51=makeQuery(id+"F0.imprint","IMPRINT",FACE,{"disambiguationData":[TD([[makeQuery(id+"F0.imprint","IMPRINT",EDGE,{"disambiguationData":[TD([[subQ2,-1.0]])],"derivedFrom":subQ1}),1.0]])]});}
            var Q52;
            {var subQ0=sQuery(id+"F0.wireOp",EDGE,"E34");var subQ1=sQuery(id+"F0.wireOp",EDGE,"E5");var subQ2=makeQuery(id+"F0.imprint","INTERSECT",VERTEX,{"derivedFrom":[subQ1,subQ0]});Q52=makeQuery(id+"F0.imprint","IMPRINT",FACE,{"disambiguationData":[TD([[makeQuery(id+"F0.imprint","IMPRINT",EDGE,{"disambiguationData":[TD([[subQ2,-1.0]])],"derivedFrom":subQ1}),1.0]])]});}
            var Q53;
            {var subQ0=sQuery(id+"F0.wireOp",EDGE,"E33");var subQ1=sQuery(id+"F0.wireOp",EDGE,"E13");var subQ2=makeQuery(id+"F0.imprint","INTERSECT",VERTEX,{"derivedFrom":[subQ1,subQ0]});Q53=makeQuery(id+"F0.imprint","IMPRINT",FACE,{"disambiguationData":[TD([[makeQuery(id+"F0.imprint","IMPRINT",EDGE,{"disambiguationData":[TD([[subQ2,-1.0]])],"derivedFrom":subQ1}),1.0]])]});}
            var Q54;
            {var subQ0=sQuery(id+"F0.wireOp",EDGE,"E33");var subQ1=sQuery(id+"F0.wireOp",EDGE,"E14");var subQ2=makeQuery(id+"F0.imprint","INTERSECT",VERTEX,{"derivedFrom":[subQ1,subQ0]});Q54=makeQuery(id+"F0.imprint","IMPRINT",FACE,{"disambiguationData":[TD([[makeQuery(id+"F0.imprint","IMPRINT",EDGE,{"disambiguationData":[TD([[subQ2,-1.0]])],"derivedFrom":subQ1}),1.0]])]});}
            var Q55;
            {var subQ0=sQuery(id+"F0.wireOp",EDGE,"E33");var subQ1=sQuery(id+"F0.wireOp",EDGE,"E28");var subQ2=makeQuery(id+"F0.imprint","INTERSECT",VERTEX,{"derivedFrom":[subQ1,subQ0]});Q55=makeQuery(id+"F0.imprint","IMPRINT",FACE,{"disambiguationData":[TD([[makeQuery(id+"F0.imprint","IMPRINT",EDGE,{"disambiguationData":[TD([[subQ2,-1.0]])],"derivedFrom":subQ1}),1.0]])]});}
            var Q56;
            {var subQ0=sQuery(id+"F0.wireOp",EDGE,"E31");var subQ1=sQuery(id+"F0.wireOp",EDGE,"E13");var subQ2=makeQuery(id+"F0.imprint","INTERSECT",VERTEX,{"derivedFrom":[subQ1,subQ0]});Q56=makeQuery(id+"F0.imprint","IMPRINT",FACE,{"disambiguationData":[TD([[makeQuery(id+"F0.imprint","IMPRINT",EDGE,{"disambiguationData":[TD([[subQ2,-1.0]])],"derivedFrom":subQ1}),1.0]])]});}
            var Q57;
            {var subQ0=sQuery(id+"F0.wireOp",EDGE,"E32");var subQ1=sQuery(id+"F0.wireOp",EDGE,"E13");var subQ2=makeQuery(id+"F0.imprint","INTERSECT",VERTEX,{"derivedFrom":[subQ1,subQ0]});Q57=makeQuery(id+"F0.imprint","IMPRINT",FACE,{"disambiguationData":[TD([[makeQuery(id+"F0.imprint","IMPRINT",EDGE,{"disambiguationData":[TD([[subQ2,-1.0]])],"derivedFrom":subQ1}),1.0]])]});}
            var Q58;
            {var subQ0=sQuery(id+"F0.wireOp",EDGE,"E33");var subQ1=sQuery(id+"F0.wireOp",EDGE,"E5");var subQ2=makeQuery(id+"F0.imprint","INTERSECT",VERTEX,{"derivedFrom":[subQ1,subQ0]});Q58=makeQuery(id+"F0.imprint","IMPRINT",FACE,{"disambiguationData":[TD([[makeQuery(id+"F0.imprint","IMPRINT",EDGE,{"disambiguationData":[TD([[subQ2,-1.0]])],"derivedFrom":subQ1}),1.0]])]});}
            var Q59;
            {var subQ0=sQuery(id+"F0.wireOp",EDGE,"E32");var subQ1=sQuery(id+"F0.wireOp",EDGE,"E5");var subQ2=makeQuery(id+"F0.imprint","INTERSECT",VERTEX,{"derivedFrom":[subQ1,subQ0]});Q59=makeQuery(id+"F0.imprint","IMPRINT",FACE,{"disambiguationData":[TD([[makeQuery(id+"F0.imprint","IMPRINT",EDGE,{"disambiguationData":[TD([[subQ2,-1.0]])],"derivedFrom":subQ1}),1.0]])]});}
            var Q60;
            {var subQ0=sQuery(id+"F0.wireOp",EDGE,"E31");var subQ1=sQuery(id+"F0.wireOp",EDGE,"E5");var subQ2=makeQuery(id+"F0.imprint","INTERSECT",VERTEX,{"derivedFrom":[subQ1,subQ0]});Q60=makeQuery(id+"F0.imprint","IMPRINT",FACE,{"disambiguationData":[TD([[makeQuery(id+"F0.imprint","IMPRINT",EDGE,{"disambiguationData":[TD([[subQ2,-1.0]])],"derivedFrom":subQ1}),1.0]])]});}
            var Q61;
            {var subQ0=sQuery(id+"F0.wireOp",EDGE,"E30");var subQ1=sQuery(id+"F0.wireOp",EDGE,"E5");var subQ2=makeQuery(id+"F0.imprint","INTERSECT",VERTEX,{"derivedFrom":[subQ1,subQ0]});Q61=makeQuery(id+"F0.imprint","IMPRINT",FACE,{"disambiguationData":[TD([[makeQuery(id+"F0.imprint","IMPRINT",EDGE,{"disambiguationData":[TD([[subQ2,-1.0]])],"derivedFrom":subQ1}),1.0]])]});}
            var Q62;
            {var subQ0=sQuery(id+"F0.wireOp",EDGE,"E30");var subQ1=sQuery(id+"F0.wireOp",EDGE,"E13");var subQ2=makeQuery(id+"F0.imprint","INTERSECT",VERTEX,{"derivedFrom":[subQ1,subQ0]});Q62=makeQuery(id+"F0.imprint","IMPRINT",FACE,{"disambiguationData":[TD([[makeQuery(id+"F0.imprint","IMPRINT",EDGE,{"disambiguationData":[TD([[subQ2,-1.0]])],"derivedFrom":subQ1}),1.0]])]});}
            var Q63;
            {var subQ1=sQuery(id+"F0.wireOp",EDGE,"E4");var subQ3=sQuery(id+"F0.wireOp",EDGE,"E14");var subQ4=makeQuery(id+"F0.imprint","INTERSECT",VERTEX,{"derivedFrom":[subQ1,subQ3]});Q63=makeQuery(id+"F0.imprint","IMPRINT",FACE,{"disambiguationData":[TD([[makeQuery(id+"F0.imprint","IMPRINT",EDGE,{"disambiguationData":[TD([[subQ4,-1.0]])],"derivedFrom":subQ3}),1.0]])]});}
            var Q64;
            {var subQ0=sQuery(id+"F0.wireOp",EDGE,"E32");var subQ1=sQuery(id+"F0.wireOp",EDGE,"E14");var subQ2=makeQuery(id+"F0.imprint","INTERSECT",VERTEX,{"derivedFrom":[subQ1,subQ0]});Q64=makeQuery(id+"F0.imprint","IMPRINT",FACE,{"disambiguationData":[TD([[makeQuery(id+"F0.imprint","IMPRINT",EDGE,{"disambiguationData":[TD([[subQ2,-1.0]])],"derivedFrom":subQ1}),1.0]])]});}
            var Q65;
            {var subQ0=sQuery(id+"F0.wireOp",EDGE,"E23.trimOffspring");var subQ1=sQuery(id+"F0.wireOp",EDGE,"E2");var subQ2=makeQuery(id+"F0.imprint","INTERSECT",VERTEX,{"derivedFrom":[subQ1,subQ0]});Q65=makeQuery(id+"F0.imprint","IMPRINT",FACE,{"disambiguationData":[TD([[makeQuery(id+"F0.imprint","IMPRINT",EDGE,{"disambiguationData":[TD([[subQ2,-1.0]])],"derivedFrom":subQ1}),-1.0]])]});}
            var Q66;
            {var subQ0=sQuery(id+"F0.wireOp",EDGE,"E12");var subQ1=sQuery(id+"F0.wireOp",EDGE,"E2");var subQ2=makeQuery(id+"F0.imprint","INTERSECT",VERTEX,{"derivedFrom":[subQ1,subQ0]});Q66=makeQuery(id+"F0.imprint","IMPRINT",FACE,{"disambiguationData":[TD([[makeQuery(id+"F0.imprint","IMPRINT",EDGE,{"disambiguationData":[TD([[subQ2,-1.0]])],"derivedFrom":subQ1}),-1.0]])]});}
            var Q67;
            {var subQ1=sQuery(id+"F0.wireOp",EDGE,"E23.trimOffspring");var subQ3=sQuery(id+"F0.wireOp",EDGE,"ySlomsGb-js9K-Jc3M-ecpa-KJbRU4JIcBsO");var subQ4=makeQuery(id+"F0.imprint","INTERSECT",VERTEX,{"derivedFrom":[subQ1,subQ3]});Q67=makeQuery(id+"F0.imprint","IMPRINT",FACE,{"disambiguationData":[TD([[makeQuery(id+"F0.imprint","IMPRINT",EDGE,{"disambiguationData":[TD([[subQ4,-1.0]])],"derivedFrom":subQ3}),-1.0]])]});}
            var Q68;
            {var subQ1=sQuery(id+"F0.wireOp",EDGE,"E12");var subQ3=sQuery(id+"F0.wireOp",EDGE,"ySlomsGb-js9K-Jc3M-ecpa-KJbRU4JIcBsO");var subQ4=makeQuery(id+"F0.imprint","INTERSECT",VERTEX,{"derivedFrom":[subQ1,subQ3]});Q68=makeQuery(id+"F0.imprint","IMPRINT",FACE,{"disambiguationData":[TD([[makeQuery(id+"F0.imprint","IMPRINT",EDGE,{"disambiguationData":[TD([[subQ4,-1.0]])],"derivedFrom":subQ3}),-1.0]])]});}
            var Q69;
            {var subQ0=sQuery(id+"F0.wireOp",EDGE,"E32");var subQ1=sQuery(id+"F0.wireOp",EDGE,"lfVSc5wO-GHd6-1YIc-mb3Z-fNhNrwEVWLqH");var subQ2=makeQuery(id+"F0.imprint","INTERSECT",VERTEX,{"derivedFrom":[subQ1,subQ0]});Q69=makeQuery(id+"F0.imprint","IMPRINT",FACE,{"disambiguationData":[TD([[makeQuery(id+"F0.imprint","IMPRINT",EDGE,{"disambiguationData":[TD([[subQ2,-1.0]])],"derivedFrom":subQ1}),1.0]])]});}
            var Q70;
            {var subQ0=sQuery(id+"F0.wireOp",EDGE,"E31");var subQ1=sQuery(id+"F0.wireOp",EDGE,"E14");var subQ2=makeQuery(id+"F0.imprint","INTERSECT",VERTEX,{"derivedFrom":[subQ1,subQ0]});Q70=makeQuery(id+"F0.imprint","IMPRINT",FACE,{"disambiguationData":[TD([[makeQuery(id+"F0.imprint","IMPRINT",EDGE,{"disambiguationData":[TD([[subQ2,-1.0]])],"derivedFrom":subQ1}),1.0]])]});}
            var Q71;
            {var subQ0=sQuery(id+"F0.wireOp",EDGE,"E30");var subQ1=sQuery(id+"F0.wireOp",EDGE,"E14");var subQ2=makeQuery(id+"F0.imprint","INTERSECT",VERTEX,{"derivedFrom":[subQ1,subQ0]});Q71=makeQuery(id+"F0.imprint","IMPRINT",FACE,{"disambiguationData":[TD([[makeQuery(id+"F0.imprint","IMPRINT",EDGE,{"disambiguationData":[TD([[subQ2,-1.0]])],"derivedFrom":subQ1}),1.0]])]});}
            var Q72;
            {var subQ0=sQuery(id+"F0.wireOp",EDGE,"E32");var subQ1=sQuery(id+"F0.wireOp",EDGE,"lfVSc5wO-GHd6-1YIc-mb3Z-fNhNrwEVWLqH");var subQ2=makeQuery(id+"F0.imprint","INTERSECT",VERTEX,{"derivedFrom":[subQ1,subQ0]});Q72=makeQuery(id+"F0.imprint","IMPRINT",FACE,{"disambiguationData":[TD([[makeQuery(id+"F0.imprint","IMPRINT",EDGE,{"disambiguationData":[TD([[subQ2,-1.0]])],"derivedFrom":subQ1}),-1.0]])]});}
            var Q73;
            {var subQ0=sQuery(id+"F0.wireOp",EDGE,"E32");var subQ1=sQuery(id+"F0.wireOp",EDGE,"E28");var subQ2=makeQuery(id+"F0.imprint","INTERSECT",VERTEX,{"derivedFrom":[subQ1,subQ0]});Q73=makeQuery(id+"F0.imprint","IMPRINT",FACE,{"disambiguationData":[TD([[makeQuery(id+"F0.imprint","IMPRINT",EDGE,{"disambiguationData":[TD([[subQ2,-1.0]])],"derivedFrom":subQ1}),1.0]])]});}
            var Q74;
            {var subQ0=sQuery(id+"F0.wireOp",EDGE,"E31");var subQ5=sQuery(id+"F0.wireOp",EDGE,"ZUNuRMhS-ujy8-TC27-MlvK-OisAggV88Hkc");var subQ6=makeQuery(id+"F0.imprint","INTERSECT",VERTEX,{"derivedFrom":[subQ0,subQ5]});Q74=makeQuery(id+"F0.imprint","IMPRINT",FACE,{"disambiguationData":[TD([[makeQuery(id+"F0.imprint","IMPRINT",EDGE,{"disambiguationData":[TD([[subQ6,1.0]])],"derivedFrom":subQ5}),-1.0]])]});}
            var Q75;
            {var subQ0=sQuery(id+"F0.wireOp",EDGE,"E30");var subQ5=sQuery(id+"F0.wireOp",EDGE,"ZUNuRMhS-ujy8-TC27-MlvK-OisAggV88Hkc");var subQ6=makeQuery(id+"F0.imprint","INTERSECT",VERTEX,{"derivedFrom":[subQ0,subQ5]});Q75=makeQuery(id+"F0.imprint","IMPRINT",FACE,{"disambiguationData":[TD([[makeQuery(id+"F0.imprint","IMPRINT",EDGE,{"disambiguationData":[TD([[subQ6,1.0]])],"derivedFrom":subQ5}),-1.0]])]});}
            var Q76;
            {var subQ1=sQuery(id+"F0.wireOp",EDGE,"E2");var subQ3=sQuery(id+"F0.wireOp",EDGE,"E12");var subQ4=makeQuery(id+"F0.imprint","INTERSECT",VERTEX,{"derivedFrom":[subQ1,subQ3]});Q76=makeQuery(id+"F0.imprint","IMPRINT",FACE,{"disambiguationData":[TD([[makeQuery(id+"F0.imprint","IMPRINT",EDGE,{"disambiguationData":[TD([[subQ4,-1.0]])],"derivedFrom":subQ3}),-1.0]])]});}
            var Q77;
            {var subQ1=sQuery(id+"F0.wireOp",EDGE,"E12");var subQ3=sQuery(id+"F0.wireOp",EDGE,"ySlomsGb-js9K-Jc3M-ecpa-KJbRU4JIcBsO");var subQ4=makeQuery(id+"F0.imprint","INTERSECT",VERTEX,{"derivedFrom":[subQ1,subQ3]});Q77=makeQuery(id+"F0.imprint","IMPRINT",FACE,{"disambiguationData":[TD([[makeQuery(id+"F0.imprint","IMPRINT",EDGE,{"disambiguationData":[TD([[subQ4,-1.0]])],"derivedFrom":subQ1}),-1.0]])]});}
            var Q78;
            {var subQ0=sQuery(id+"F0.wireOp",EDGE,"ZUNuRMhS-ujy8-TC27-MlvK-OisAggV88Hkc");var subQ3=sQuery(id+"F0.wireOp",EDGE,"E30");var subQ5=makeQuery(id+"F0.imprint","INTERSECT",VERTEX,{"derivedFrom":[subQ3,subQ0]});Q78=makeQuery(id+"F0.imprint","IMPRINT",FACE,{"disambiguationData":[TD([[makeQuery(id+"F0.imprint","IMPRINT",EDGE,{"disambiguationData":[TD([[subQ5,1.0]])],"derivedFrom":subQ3}),-1.0]])]});}
            var Q79;
            {var subQ1=sQuery(id+"F0.wireOp",EDGE,"lfVSc5wO-GHd6-1YIc-mb3Z-fNhNrwEVWLqH");var subQ3=sQuery(id+"F0.wireOp",EDGE,"E30");var subQ4=makeQuery(id+"F0.imprint","INTERSECT",VERTEX,{"derivedFrom":[subQ1,subQ3]});Q79=makeQuery(id+"F0.imprint","IMPRINT",FACE,{"disambiguationData":[TD([[makeQuery(id+"F0.imprint","IMPRINT",EDGE,{"disambiguationData":[TD([[subQ4,1.0]])],"derivedFrom":subQ3}),-1.0]])]});}
            var Q80;
            {var subQ1=sQuery(id+"F0.wireOp",EDGE,"lfVSc5wO-GHd6-1YIc-mb3Z-fNhNrwEVWLqH");var subQ3=sQuery(id+"F0.wireOp",EDGE,"E30");var subQ4=makeQuery(id+"F0.imprint","INTERSECT",VERTEX,{"derivedFrom":[subQ1,subQ3]});Q80=makeQuery(id+"F0.imprint","IMPRINT",FACE,{"disambiguationData":[TD([[makeQuery(id+"F0.imprint","IMPRINT",EDGE,{"disambiguationData":[TD([[subQ4,-1.0]])],"derivedFrom":subQ3}),-1.0]])]});}
            var Q81;
            {var subQ1=sQuery(id+"F0.wireOp",EDGE,"E28");var subQ3=sQuery(id+"F0.wireOp",EDGE,"E30");var subQ4=makeQuery(id+"F0.imprint","INTERSECT",VERTEX,{"derivedFrom":[subQ1,subQ3]});Q81=makeQuery(id+"F0.imprint","IMPRINT",FACE,{"disambiguationData":[TD([[makeQuery(id+"F0.imprint","IMPRINT",EDGE,{"disambiguationData":[TD([[subQ4,1.0]])],"derivedFrom":subQ3}),-1.0]])]});}
            var Q82;
            {var subQ0=sQuery(id+"F0.wireOp",EDGE,"E30");var subQ1=sQuery(id+"F0.wireOp",EDGE,"lfVSc5wO-GHd6-1YIc-mb3Z-fNhNrwEVWLqH");var subQ2=makeQuery(id+"F0.imprint","INTERSECT",VERTEX,{"derivedFrom":[subQ1,subQ0]});Q82=makeQuery(id+"F0.imprint","IMPRINT",FACE,{"disambiguationData":[TD([[makeQuery(id+"F0.imprint","IMPRINT",EDGE,{"disambiguationData":[TD([[subQ2,-1.0]])],"derivedFrom":subQ1}),-1.0]])]});}
            var Q83;
            {var subQ0=sQuery(id+"F0.wireOp",EDGE,"E31");var subQ1=sQuery(id+"F0.wireOp",EDGE,"lfVSc5wO-GHd6-1YIc-mb3Z-fNhNrwEVWLqH");var subQ2=makeQuery(id+"F0.imprint","INTERSECT",VERTEX,{"derivedFrom":[subQ1,subQ0]});Q83=makeQuery(id+"F0.imprint","IMPRINT",FACE,{"disambiguationData":[TD([[makeQuery(id+"F0.imprint","IMPRINT",EDGE,{"disambiguationData":[TD([[subQ2,-1.0]])],"derivedFrom":subQ1}),-1.0]])]});}
            var Q84;
            {var subQ0=sQuery(id+"F0.wireOp",EDGE,"E30");var subQ1=sQuery(id+"F0.wireOp",EDGE,"E28");var subQ2=makeQuery(id+"F0.imprint","INTERSECT",VERTEX,{"derivedFrom":[subQ1,subQ0]});Q84=makeQuery(id+"F0.imprint","IMPRINT",FACE,{"disambiguationData":[TD([[makeQuery(id+"F0.imprint","IMPRINT",EDGE,{"disambiguationData":[TD([[subQ2,-1.0]])],"derivedFrom":subQ1}),1.0]])]});}
            var Q85;
            {var subQ0=sQuery(id+"F0.wireOp",EDGE,"E30");var subQ1=sQuery(id+"F0.wireOp",EDGE,"lfVSc5wO-GHd6-1YIc-mb3Z-fNhNrwEVWLqH");var subQ2=makeQuery(id+"F0.imprint","INTERSECT",VERTEX,{"derivedFrom":[subQ1,subQ0]});Q85=makeQuery(id+"F0.imprint","IMPRINT",FACE,{"disambiguationData":[TD([[makeQuery(id+"F0.imprint","IMPRINT",EDGE,{"disambiguationData":[TD([[subQ2,-1.0]])],"derivedFrom":subQ1}),1.0]])]});}
            var Q86;
            {var subQ0=sQuery(id+"F0.wireOp",EDGE,"E31");var subQ1=sQuery(id+"F0.wireOp",EDGE,"lfVSc5wO-GHd6-1YIc-mb3Z-fNhNrwEVWLqH");var subQ2=makeQuery(id+"F0.imprint","INTERSECT",VERTEX,{"derivedFrom":[subQ1,subQ0]});Q86=makeQuery(id+"F0.imprint","IMPRINT",FACE,{"disambiguationData":[TD([[makeQuery(id+"F0.imprint","IMPRINT",EDGE,{"disambiguationData":[TD([[subQ2,-1.0]])],"derivedFrom":subQ1}),1.0]])]});}
            var Q87;
            {var subQ0=sQuery(id+"F0.wireOp",EDGE,"E31");var subQ1=sQuery(id+"F0.wireOp",EDGE,"E28");var subQ2=makeQuery(id+"F0.imprint","INTERSECT",VERTEX,{"derivedFrom":[subQ1,subQ0]});Q87=makeQuery(id+"F0.imprint","IMPRINT",FACE,{"disambiguationData":[TD([[makeQuery(id+"F0.imprint","IMPRINT",EDGE,{"disambiguationData":[TD([[subQ2,-1.0]])],"derivedFrom":subQ1}),1.0]])]});}
            var Q88;
            {var subQ1=sQuery(id+"F0.wireOp",EDGE,"E7");var subQ3=sQuery(id+"F0.wireOp",EDGE,"E38");var subQ4=makeQuery(id+"F0.imprint","INTERSECT",VERTEX,{"derivedFrom":[subQ1,subQ3]});Q88=makeQuery(id+"F0.imprint","IMPRINT",FACE,{"disambiguationData":[TD([[makeQuery(id+"F0.imprint","IMPRINT",EDGE,{"disambiguationData":[TD([[subQ4,1.0]])],"derivedFrom":subQ3}),-1.0]])]});}
            var Q89;
            {var subQ1=sQuery(id+"F0.wireOp",EDGE,"E25.trimOffspring");var subQ3=sQuery(id+"F0.wireOp",EDGE,"E38");var subQ4=makeQuery(id+"F0.imprint","INTERSECT",VERTEX,{"derivedFrom":[subQ1,subQ3]});Q89=makeQuery(id+"F0.imprint","IMPRINT",FACE,{"disambiguationData":[TD([[makeQuery(id+"F0.imprint","IMPRINT",EDGE,{"disambiguationData":[TD([[subQ4,1.0]])],"derivedFrom":subQ3}),-1.0]])]});}
            var Q90;
            {var subQ1=sQuery(id+"F0.wireOp",EDGE,"E23.trimOffspring");var subQ3=sQuery(id+"F0.wireOp",EDGE,"E38");var subQ4=makeQuery(id+"F0.imprint","INTERSECT",VERTEX,{"derivedFrom":[subQ1,subQ3]});Q90=makeQuery(id+"F0.imprint","IMPRINT",FACE,{"disambiguationData":[TD([[makeQuery(id+"F0.imprint","IMPRINT",EDGE,{"disambiguationData":[TD([[subQ4,-1.0]])],"derivedFrom":subQ3}),-1.0]])]});}
            var Q91;
            {var subQ1=sQuery(id+"F0.wireOp",EDGE,"E12");var subQ3=sQuery(id+"F0.wireOp",EDGE,"E38");var subQ4=makeQuery(id+"F0.imprint","INTERSECT",VERTEX,{"derivedFrom":[subQ1,subQ3]});Q91=makeQuery(id+"F0.imprint","IMPRINT",FACE,{"disambiguationData":[TD([[makeQuery(id+"F0.imprint","IMPRINT",EDGE,{"disambiguationData":[TD([[subQ4,-1.0]])],"derivedFrom":subQ3}),-1.0]])]});}
            var Q92;
            {var subQ1=sQuery(id+"F0.wireOp",EDGE,"E30");var subQ3=sQuery(id+"F0.wireOp",EDGE,"E37");var subQ4=makeQuery(id+"F0.imprint","INTERSECT",VERTEX,{"derivedFrom":[subQ1,subQ3]});Q92=makeQuery(id+"F0.imprint","IMPRINT",FACE,{"disambiguationData":[TD([[makeQuery(id+"F0.imprint","IMPRINT",EDGE,{"disambiguationData":[TD([[subQ4,1.0]])],"derivedFrom":subQ3}),-1.0]])]});}
            var Q93;
            {var subQ1=sQuery(id+"F0.wireOp",EDGE,"E32");var subQ3=sQuery(id+"F0.wireOp",EDGE,"E37");var subQ4=makeQuery(id+"F0.imprint","INTERSECT",VERTEX,{"derivedFrom":[subQ1,subQ3]});Q93=makeQuery(id+"F0.imprint","IMPRINT",FACE,{"disambiguationData":[TD([[makeQuery(id+"F0.imprint","IMPRINT",EDGE,{"disambiguationData":[TD([[subQ4,1.0]])],"derivedFrom":subQ3}),-1.0]])]});}
            var Q94;
            {var subQ1=sQuery(id+"F0.wireOp",EDGE,"E31");var subQ3=sQuery(id+"F0.wireOp",EDGE,"E37");var subQ4=makeQuery(id+"F0.imprint","INTERSECT",VERTEX,{"derivedFrom":[subQ1,subQ3]});Q94=makeQuery(id+"F0.imprint","IMPRINT",FACE,{"disambiguationData":[TD([[makeQuery(id+"F0.imprint","IMPRINT",EDGE,{"disambiguationData":[TD([[subQ4,1.0]])],"derivedFrom":subQ3}),-1.0]])]});}
            var Q95;
            {var subQ1=sQuery(id+"F0.wireOp",EDGE,"E33");var subQ3=sQuery(id+"F0.wireOp",EDGE,"E37");var subQ4=makeQuery(id+"F0.imprint","INTERSECT",VERTEX,{"derivedFrom":[subQ1,subQ3]});Q95=makeQuery(id+"F0.imprint","IMPRINT",FACE,{"disambiguationData":[TD([[makeQuery(id+"F0.imprint","IMPRINT",EDGE,{"disambiguationData":[TD([[subQ4,1.0]])],"derivedFrom":subQ3}),-1.0]])]});}
            var Q96;
            {var subQ0=sQuery(id+"F0.wireOp",EDGE,"E8");Q96=makeQuery(id+"F0.imprint","IMPRINT",FACE,{"disambiguationData":[TD([[makeQuery(id+"F0.imprint","IMPRINT",EDGE,{"derivedFrom":subQ0}),-1.0]])]});}
            var Q97;
            {var subQ1=sQuery(id+"F0.wireOp",EDGE,"E7");var subQ3=sQuery(id+"F0.wireOp",EDGE,"E35");var subQ4=makeQuery(id+"F0.imprint","INTERSECT",VERTEX,{"derivedFrom":[subQ1,subQ3]});Q97=makeQuery(id+"F0.imprint","IMPRINT",FACE,{"disambiguationData":[TD([[makeQuery(id+"F0.imprint","IMPRINT",EDGE,{"disambiguationData":[TD([[subQ4,1.0]])],"derivedFrom":subQ3}),-1.0]])]});}
            var Q98;
            {var subQ0=sQuery(id+"F0.wireOp",EDGE,"E37");var subQ1=sQuery(id+"F0.wireOp",EDGE,"E33");var subQ2=makeQuery(id+"F0.imprint","INTERSECT",VERTEX,{"derivedFrom":[subQ1,subQ0]});Q98=makeQuery(id+"F0.imprint","IMPRINT",FACE,{"disambiguationData":[TD([[makeQuery(id+"F0.imprint","IMPRINT",EDGE,{"disambiguationData":[TD([[subQ2,-1.0]])],"derivedFrom":subQ1}),1.0]])]});}
            var Q99;
            {var subQ0=sQuery(id+"F0.wireOp",EDGE,"E37");var subQ1=sQuery(id+"F0.wireOp",EDGE,"E32");var subQ2=makeQuery(id+"F0.imprint","INTERSECT",VERTEX,{"derivedFrom":[subQ1,subQ0]});Q99=makeQuery(id+"F0.imprint","IMPRINT",FACE,{"disambiguationData":[TD([[makeQuery(id+"F0.imprint","IMPRINT",EDGE,{"disambiguationData":[TD([[subQ2,-1.0]])],"derivedFrom":subQ1}),1.0]])]});}
            var Q100;
            {var subQ0=sQuery(id+"F0.wireOp",EDGE,"E37");var subQ1=sQuery(id+"F0.wireOp",EDGE,"E31");var subQ2=makeQuery(id+"F0.imprint","INTERSECT",VERTEX,{"derivedFrom":[subQ1,subQ0]});Q100=makeQuery(id+"F0.imprint","IMPRINT",FACE,{"disambiguationData":[TD([[makeQuery(id+"F0.imprint","IMPRINT",EDGE,{"disambiguationData":[TD([[subQ2,-1.0]])],"derivedFrom":subQ1}),1.0]])]});}
            var Q101;
            {var subQ0=sQuery(id+"F0.wireOp",EDGE,"E37");var subQ1=sQuery(id+"F0.wireOp",EDGE,"E30");var subQ2=makeQuery(id+"F0.imprint","INTERSECT",VERTEX,{"derivedFrom":[subQ1,subQ0]});Q101=makeQuery(id+"F0.imprint","IMPRINT",FACE,{"disambiguationData":[TD([[makeQuery(id+"F0.imprint","IMPRINT",EDGE,{"disambiguationData":[TD([[subQ2,-1.0]])],"derivedFrom":subQ1}),1.0]])]});}
            extrude(context, id + "F1", {"entities" : qUnion([Q0, Q1, Q2, Q3, Q4, Q5, Q6, Q7, Q8, Q9, Q10, Q11, Q12, Q13, Q14, Q15, Q16, Q17, Q18, Q19, Q20, Q21, Q22, Q23, Q24, Q25, Q26, Q27, Q28, Q29, Q30, Q31, Q32, Q33, Q34, Q35, Q36, Q37, Q38, Q39, Q40, Q41, Q42, Q43, Q44, Q45, Q46, Q47, Q48, Q49, Q50, Q51, Q52, Q53, Q54, Q55, Q56, Q57, Q58, Q59, Q60, Q61, Q62, Q63, Q64, Q65, Q66, Q67, Q68, Q69, Q70, Q71, Q72, Q73, Q74, Q75, Q76, Q77, Q78, Q79, Q80, Q81, Q82, Q83, Q84, Q85, Q86, Q87, Q88, Q89, Q90, Q91, Q92, Q93, Q94, Q95, Q96, Q97, Q98, Q99, Q100, Q101]), "oppositeDirection" : true, "depth" : 152.4 * mm, "offsetDistance" : 25 * mm});
        }
        {
            var Q0;
            Q0=makeQuery(id+"F1.opExtrude","CAP_FACE",FACE,{"disambiguationData":[OSD([sQuery(id+"F0.wireOp",EDGE,"E0"),sQuery(id+"F0.wireOp",EDGE,"E1"),sQuery(id+"F0.wireOp",EDGE,"E3"),sQuery(id+"F0.wireOp",EDGE,"E4"),sQuery(id+"F0.wireOp",EDGE,"E5"),sQuery(id+"F0.wireOp",EDGE,"E6"),sQuery(id+"F0.wireOp",EDGE,"E7"),sQuery(id+"F0.wireOp",EDGE,"E8"),sQuery(id+"F0.wireOp",EDGE,"E16"),sQuery(id+"F0.wireOp",EDGE,"E21"),sQuery(id+"F0.wireOp",EDGE,"E23.trimOffspring"),sQuery(id+"F0.wireOp",EDGE,"E24.trimOffspring"),sQuery(id+"F0.wireOp",EDGE,"E27")])],"isStart":false});
            var sketch = newSketch(context, id + "F2", { "sketchPlane" : qUnion([Q0])});
            skLineSegment(sketch, "E40", {"start": v(-9949.45, -5796.23) * mm, "end": v(-9820.93, -5878.15) * mm});
            skLineSegment(sketch, "E41", {"start": v(-9820.93, -5878.15) * mm, "end": v(-9902.85, -6006.66) * mm});
            skLineSegment(sketch, "E42", {"start": v(-9902.85, -6006.66) * mm, "end": v(-10031.37, -5924.74) * mm});
            skLineSegment(sketch, "E43", {"start": v(-10031.37, -5924.74) * mm, "end": v(-9949.45, -5796.23) * mm});
            skLineSegment(sketch, "E44", {"start": v(-5733.23, -8483.9) * mm, "end": v(-5861.74, -8401.97) * mm});
            skLineSegment(sketch, "E45", {"start": v(-5861.74, -8401.97) * mm, "end": v(-5943.66, -8530.48) * mm});
            skLineSegment(sketch, "E46", {"start": v(-5943.66, -8530.48) * mm, "end": v(-5815.15, -8612.4) * mm});
            skLineSegment(sketch, "E47", {"start": v(-5815.15, -8612.4) * mm, "end": v(-5733.23, -8483.9) * mm});
            skLineSegment(sketch, "E48", {"start": v(-8336.85, -3266.5) * mm, "end": v(-8254.93, -3137.99) * mm});
            skLineSegment(sketch, "E49", {"start": v(-8254.93, -3137.99) * mm, "end": v(-8126.42, -3219.9) * mm});
            skLineSegment(sketch, "E50", {"start": v(-8126.42, -3219.9) * mm, "end": v(-8208.34, -3348.42) * mm});
            skLineSegment(sketch, "E51", {"start": v(-8208.34, -3348.42) * mm, "end": v(-8336.85, -3266.5) * mm});
            skLineSegment(sketch, "E52", {"start": v(-4120.63, -5954.16) * mm, "end": v(-4120.63, -5954.16) * mm});
            skLineSegment(sketch, "E53", {"start": v(-4120.63, -5954.16) * mm, "end": v(-4153.58, -5805.37) * mm});
            skLineSegment(sketch, "E54", {"start": v(-4153.58, -5805.37) * mm, "end": v(-4004.78, -5772.42) * mm});
            skLineSegment(sketch, "E55", {"start": v(-4004.78, -5772.42) * mm, "end": v(-4120.63, -5954.16) * mm});
            skLineSegment(sketch, "E56", {"start": v(1012.71, -12784.15) * mm, "end": v(884.2, -12702.23) * mm});
            skLineSegment(sketch, "E57", {"start": v(884.2, -12702.23) * mm, "end": v(802.28, -12830.74) * mm});
            skLineSegment(sketch, "E58", {"start": v(802.28, -12830.74) * mm, "end": v(930.8, -12912.66) * mm});
            skLineSegment(sketch, "E59", {"start": v(930.8, -12912.66) * mm, "end": v(1012.71, -12784.15) * mm});
            skLineSegment(sketch, "E60", {"start": v(6269.18, -8831.1) * mm, "end": v(6177.58, -8709.3) * mm});
            skLineSegment(sketch, "E61", {"start": v(6177.58, -8709.3) * mm, "end": v(6299.38, -8617.7) * mm});
            skLineSegment(sketch, "E62", {"start": v(6299.38, -8617.7) * mm, "end": v(6390.98, -8739.5) * mm});
            skLineSegment(sketch, "E63", {"start": v(6390.98, -8739.5) * mm, "end": v(6269.18, -8831.1) * mm});
            skLineSegment(sketch, "E64", {"start": v(932, -5061.68) * mm, "end": v(840.4, -4939.88) * mm});
            skLineSegment(sketch, "E65", {"start": v(840.4, -4939.88) * mm, "end": v(962.2, -4848.28) * mm});
            skLineSegment(sketch, "E66", {"start": v(962.2, -4848.28) * mm, "end": v(1053.8, -4970.08) * mm});
            skLineSegment(sketch, "E67", {"start": v(1053.8, -4970.08) * mm, "end": v(932, -5061.68) * mm});
            skLineSegment(sketch, "E68", {"start": v(-2488.77, -10552.1) * mm, "end": v(-2570.69, -10680.61) * mm});
            skLineSegment(sketch, "E69", {"start": v(-2570.69, -10680.61) * mm, "end": v(-2442.18, -10762.53) * mm});
            skLineSegment(sketch, "E70", {"start": v(-2442.18, -10762.53) * mm, "end": v(-2360.26, -10634.02) * mm});
            skLineSegment(sketch, "E71", {"start": v(-2360.26, -10634.02) * mm, "end": v(-2488.77, -10552.1) * mm});
            skSolve(sketch);
        }
        {
            var Q0;
            Q0 = qSketchRegion(id + "F2", true);
            extrude(context, id + "F3", {"entities" : qUnion([Q0]), "operationType" : NewBodyOperationType.ADD, "depth" : 2500 * mm, "offsetDistance" : 25 * mm});
        }
    });
